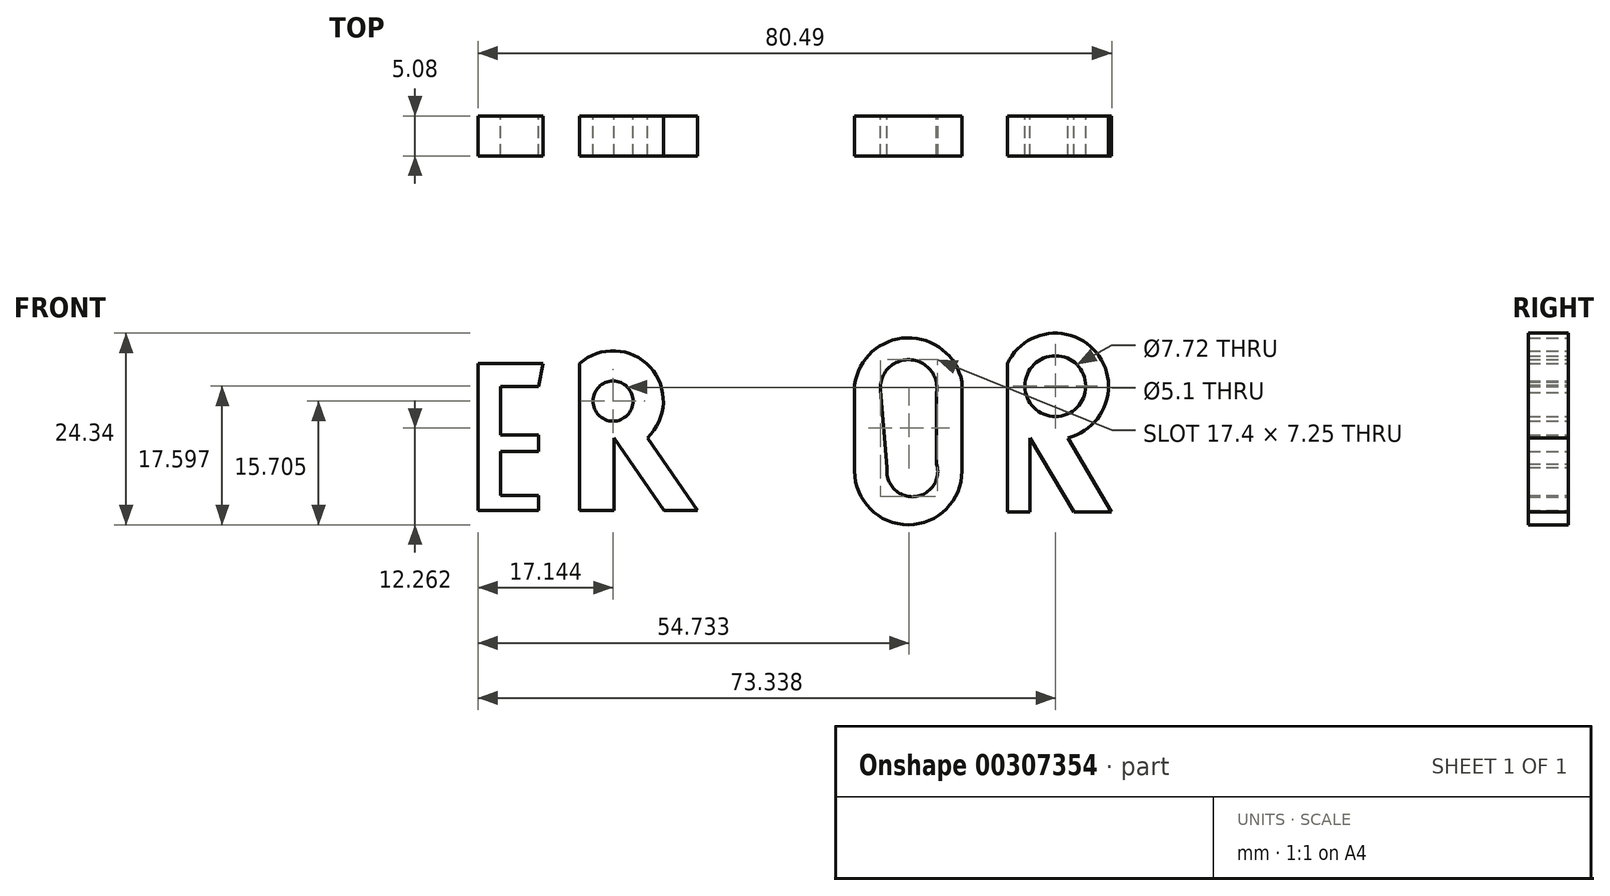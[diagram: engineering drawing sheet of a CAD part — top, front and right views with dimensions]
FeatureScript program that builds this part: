
annotation { "Feature Type Name" : "Feature", "Feature Type Description" : "" }
export const myFeature = defineFeature(function(context is Context, id is Id, definition is map)
    precondition{}
    {
        {
            var Q0;
            Q0=qCreatedBy(makeId("Front.planeOp"),FACE);
            var sketch = newSketch(context, id + "F0", { "sketchPlane" : qUnion([Q0])});
            skLineSegment(sketch, "E0", {"start": v(-42.85, 42.9) * mm, "end": v(-51.1, 42.9) * mm});
            skLineSegment(sketch, "E1", {"start": v(-51.1, 42.9) * mm, "end": v(-51.1, 33.3) * mm});
            skLineSegment(sketch, "E2", {"start": v(-51.1, 33.3) * mm, "end": v(-51.1, 24.26) * mm});
            skLineSegment(sketch, "E3", {"start": v(-51.1, 24.26) * mm, "end": v(-43.43, 24.26) * mm});
            skLineSegment(sketch, "E4", {"start": v(-43.43, 24.26) * mm, "end": v(-43.43, 26.18) * mm});
            skLineSegment(sketch, "E5", {"start": v(-43.43, 26.18) * mm, "end": v(-48.23, 26.18) * mm});
            skLineSegment(sketch, "E6", {"start": v(-48.23, 26.18) * mm, "end": v(-48.23, 31.75) * mm});
            skLineSegment(sketch, "E7", {"start": v(-48.23, 31.75) * mm, "end": v(-43.43, 31.75) * mm});
            skLineSegment(sketch, "E8", {"start": v(-43.43, 31.75) * mm, "end": v(-43.43, 33.87) * mm});
            skLineSegment(sketch, "E9", {"start": v(-43.43, 33.87) * mm, "end": v(-48.23, 33.87) * mm});
            skLineSegment(sketch, "E10", {"start": v(-48.23, 33.87) * mm, "end": v(-48.23, 40.01) * mm});
            skLineSegment(sketch, "E11", {"start": v(-48.23, 40.01) * mm, "end": v(-43.43, 40.01) * mm});
            skLineSegment(sketch, "E12", {"start": v(-43.43, 40.01) * mm, "end": v(-42.85, 42.9) * mm});
            skLineSegment(sketch, "E13", {"start": v(-38.24, 24.26) * mm, "end": v(-38.24, 42.9) * mm});
            skLineSegment(sketch, "E14", {"start": v(-38.24, 24.26) * mm, "end": v(-33.82, 24.26) * mm});
            skLineSegment(sketch, "E15", {"start": v(-33.82, 24.26) * mm, "end": v(-33.82, 33.48) * mm});
            skLineSegment(sketch, "E16", {"start": v(-33.82, 33.48) * mm, "end": v(-27.48, 24.26) * mm});
            skLineSegment(sketch, "E17", {"start": v(-27.48, 24.26) * mm, "end": v(-23.26, 24.26) * mm});
            skLineSegment(sketch, "E18", {"start": v(-23.26, 24.26) * mm, "end": v(-29.6, 33.48) * mm});
            skArc(sketch, "E19", {"start": v(-29.6, 33.48) * mm, "mid": v(-29.26, 42.47) * mm, "end": v(-38.24, 42.9) * mm});
            skCircle(sketch, "E20", {"center": v(-33.97, 38.14) * mm, "radius": 2.55 * mm});
            skLineSegment(sketch, "E21", {"start": v(-20.38, 24.07) * mm, "end": v(-20.38, 42.9) * mm});
            skLineSegment(sketch, "E22", {"start": v(-20.38, 42.9) * mm, "end": v(-20.38, 24.07) * mm});
            skLineSegment(sketch, "E23", {"start": v(-18.07, 24.07) * mm, "end": v(-18.07, 33.48) * mm});
            skPoint(sketch, "E23.endSnap0", {"position": v(-20.38, 33.48) * mm});
            skLineSegment(sketch, "E24", {"start": v(-18.07, 33.48) * mm, "end": v(-18.07, 24.07) * mm});
            skLineSegment(sketch, "E25", {"start": v(-20.38, 24.07) * mm, "end": v(-18.07, 24.07) * mm});
            skLineSegment(sketch, "E26", {"start": v(-18.07, 33.48) * mm, "end": v(-13.08, 24.07) * mm});
            skLineSegment(sketch, "E27", {"start": v(-13.08, 24.07) * mm, "end": v(-10.2, 24.07) * mm});
            skLineSegment(sketch, "E28", {"start": v(-10.2, 24.07) * mm, "end": v(-15.19, 33.48) * mm});
            skArc(sketch, "E29", {"start": v(-15.19, 33.48) * mm, "mid": v(-10.5, 42.2) * mm, "end": v(-20.38, 42.9) * mm});
            skCircle(sketch, "E30", {"center": v(-15.66, 39.36) * mm, "radius": 3.24 * mm});
            skArc(sketch, "E31", {"start": v(10.36, 40.6) * mm, "mid": v(3.38, 46.18) * mm, "end": v(-3.28, 40.2) * mm});
            skLineSegment(sketch, "E32", {"start": v(-3.28, 40.2) * mm, "end": v(-3.28, 29.26) * mm});
            skLineSegment(sketch, "E33", {"start": v(10.36, 40.6) * mm, "end": v(10.36, 29.26) * mm});
            skArc(sketch, "E34", {"start": v(-3.28, 29.26) * mm, "mid": v(3.54, 22.44) * mm, "end": v(10.36, 29.26) * mm});
            skLineSegment(sketch, "E35", {"start": v(16.12, 24.07) * mm, "end": v(16.12, 42.9) * mm});
            skLineSegment(sketch, "E36", {"start": v(16.12, 24.07) * mm, "end": v(19, 24.07) * mm});
            skLineSegment(sketch, "E37", {"start": v(19, 24.07) * mm, "end": v(19, 33.48) * mm});
            skLineSegment(sketch, "E38", {"start": v(19, 33.48) * mm, "end": v(24.57, 24.07) * mm});
            skLineSegment(sketch, "E39", {"start": v(24.57, 24.07) * mm, "end": v(29.38, 24.07) * mm});
            skLineSegment(sketch, "E40", {"start": v(29.38, 24.07) * mm, "end": v(23.8, 33.48) * mm});
            skArc(sketch, "E41", {"start": v(23.8, 33.48) * mm, "mid": v(27.45, 44.3) * mm, "end": v(16.12, 42.9) * mm});
            skCircle(sketch, "E42", {"center": v(22.23, 40.04) * mm, "radius": 3.86 * mm});
            skArc(sketch, "E43", {"start": v(7.14, 39.26) * mm, "mid": v(3.7, 43.4) * mm, "end": v(0, 39.5) * mm});
            skLineSegment(sketch, "E44", {"start": v(0, 39.5) * mm, "end": v(0.86, 29.7) * mm});
            skLineSegment(sketch, "E45", {"start": v(7.14, 39.26) * mm, "end": v(7.14, 30.18) * mm});
            skArc(sketch, "E46", {"start": v(0.86, 29.7) * mm, "mid": v(4.3, 26) * mm, "end": v(7.14, 30.18) * mm});
            skSolve(sketch);
        }
        {
            var Q0;
            Q0=makeQuery(id+"F0.imprint","IMPRINT",FACE,{"disambiguationData":[TD([[makeQuery(id+"F0.imprint","IMPRINT",EDGE,{"derivedFrom":sQuery(id+"F0.wireOp",EDGE,"E0")}),1.0]])]});
            var Q1;
            Q1=makeQuery(id+"F0.imprint","IMPRINT",FACE,{"disambiguationData":[TD([[makeQuery(id+"F0.imprint","IMPRINT",EDGE,{"derivedFrom":sQuery(id+"F0.wireOp",EDGE,"E13")}),-1.0]])]});
            var Q2;
            Q2=makeQuery(id+"F0.imprint","IMPRINT",FACE,{"disambiguationData":[TD([[makeQuery(id+"F0.imprint","IMPRINT",EDGE,{"derivedFrom":sQuery(id+"F0.wireOp",EDGE,"E22")}),1.0]])]});
            var Q3;
            Q3=makeQuery(id+"F0.imprint","IMPRINT",FACE,{"disambiguationData":[TD([[makeQuery(id+"F0.imprint","IMPRINT",EDGE,{"derivedFrom":sQuery(id+"F0.wireOp",EDGE,"E31")}),1.0]])]});
            var Q4;
            Q4=makeQuery(id+"F0.imprint","IMPRINT",FACE,{"disambiguationData":[TD([[makeQuery(id+"F0.imprint","IMPRINT",EDGE,{"derivedFrom":sQuery(id+"F0.wireOp",EDGE,"E35")}),-1.0]])]});
            extrude(context, id + "F1", {"entities" : qUnion([Q0, Q1, Q2, Q3, Q4]), "depth" : 5.08 * mm});
        }
    });
